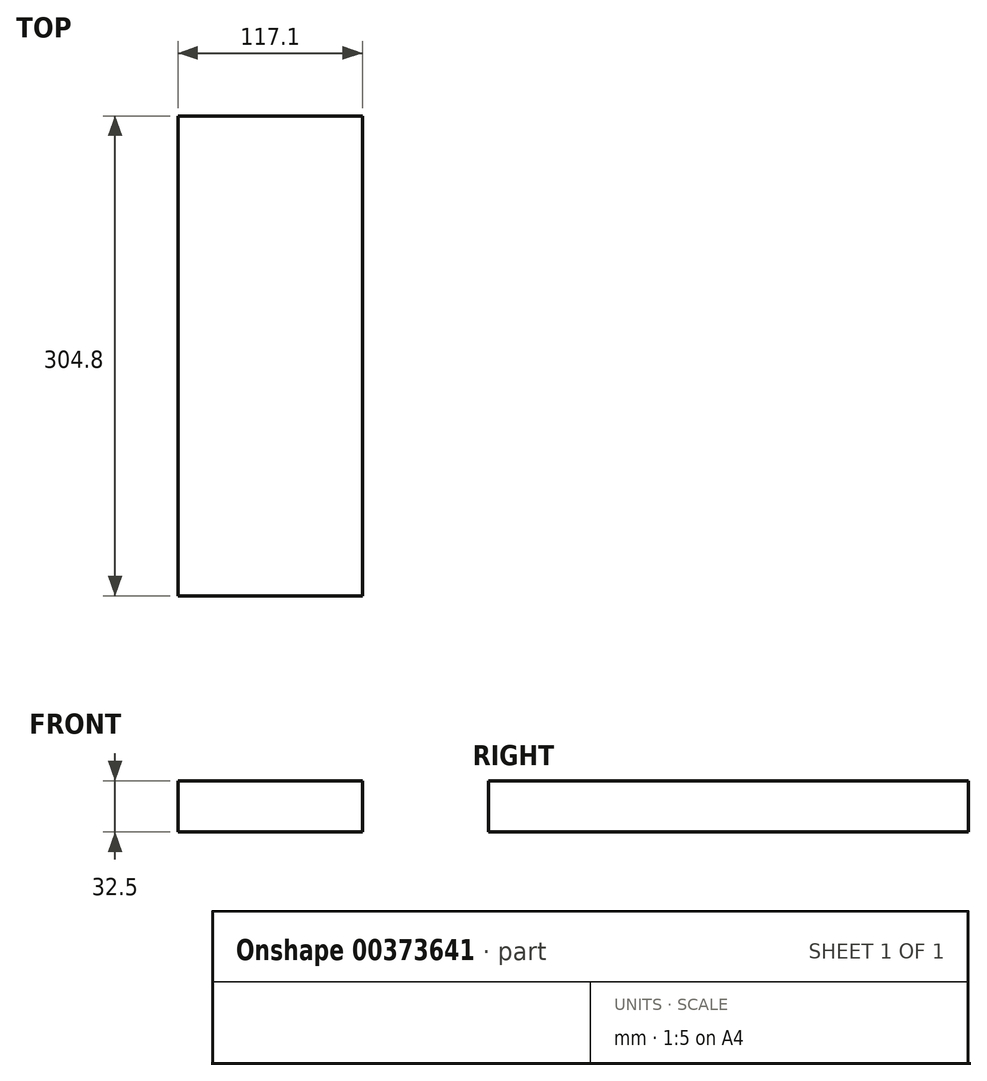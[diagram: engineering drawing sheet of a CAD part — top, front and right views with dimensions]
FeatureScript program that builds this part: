
annotation { "Feature Type Name" : "Feature", "Feature Type Description" : "" }
export const myFeature = defineFeature(function(context is Context, id is Id, definition is map)
    precondition{}
    {
        {
            var Q0;
            Q0=qCreatedBy(makeId("Front.planeOp"),FACE);
            var sketch = newSketch(context, id + "F0", { "sketchPlane" : qUnion([Q0])});
            skLineSegment(sketch, "E0.bottom", {"start": v(-58.55, 16.25) * mm, "end": v(58.55, 16.25) * mm});
            skLineSegment(sketch, "E0.top", {"start": v(-58.55, -16.25) * mm, "end": v(58.55, -16.25) * mm});
            skLineSegment(sketch, "E0.left", {"start": v(-58.55, 16.25) * mm, "end": v(-58.55, -16.25) * mm});
            skLineSegment(sketch, "E0.right", {"start": v(58.55, 16.25) * mm, "end": v(58.55, -16.25) * mm});
            skPoint(sketch, "E0.middle", {"position": v(0, 0) * mm});
            skSolve(sketch);
        }
        {
            var Q0;
            Q0=makeQuery(id+"F0.imprint","IMPRINT",FACE,{"disambiguationData":[TD([[makeQuery(id+"F0.imprint","IMPRINT",EDGE,{"derivedFrom":sQuery(id+"F0.wireOp",EDGE,"E0.bottom")}),-1.0]])]});
            extrude(context, id + "F1", {"entities" : qUnion([Q0]), "endBound" : BoundingType.SYMMETRIC, "depth" : 304.8 * mm});
        }
    });
